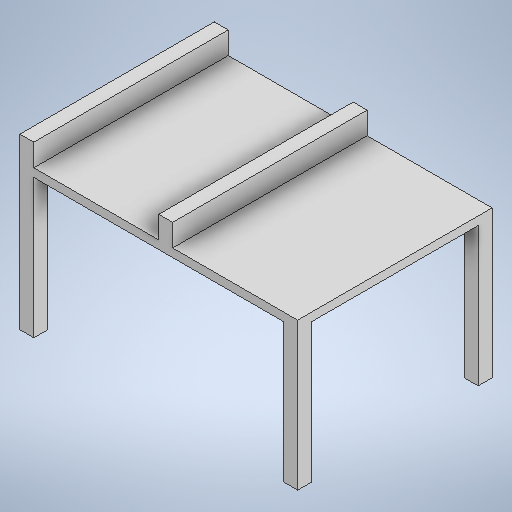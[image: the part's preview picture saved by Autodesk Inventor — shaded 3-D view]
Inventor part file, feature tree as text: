
AUTODESK INVENTOR PART (.ipt)
format: ipt  version: 2025 (Build 290162000, 162)  size: 274,944 bytes
history: native  units: in
note: dims shown in document units (in); Inventor stores cm internally (conversion verified against a paired STEP export)
features: extrude x3, sketch x2
ambient origin geometry x8: Origin, YZ Plane, XZ Plane, XY Plane, X Axis, Y Axis, Z Axis, Center Point
bodies: Solid1 (feature_tree)
feature tree (5):
  sketch  "Sketch1"  dims[d0=39.3701in d1=27.5591in]
  extrude  "Extrusion1"  Depth=27.5591in
  extrude  "Extrusion2"  Depth=1.9685in
  extrude  "Extrusion3"  Depth=1.9685in
  sketch  "Sketch2"  dims[d2=21.6535in d3=1.9685in d4=1.9685in d5=4.3307in d6=0.0in d7=1.1811in d8=0.0in d9=1.9685in d10=1.9685in d11=1.9685in d12=1.9685in d13=1.9685in d14=1.9685in d15=1.9685in d16=1.9685in d17=19.685in d18=0.0in]
